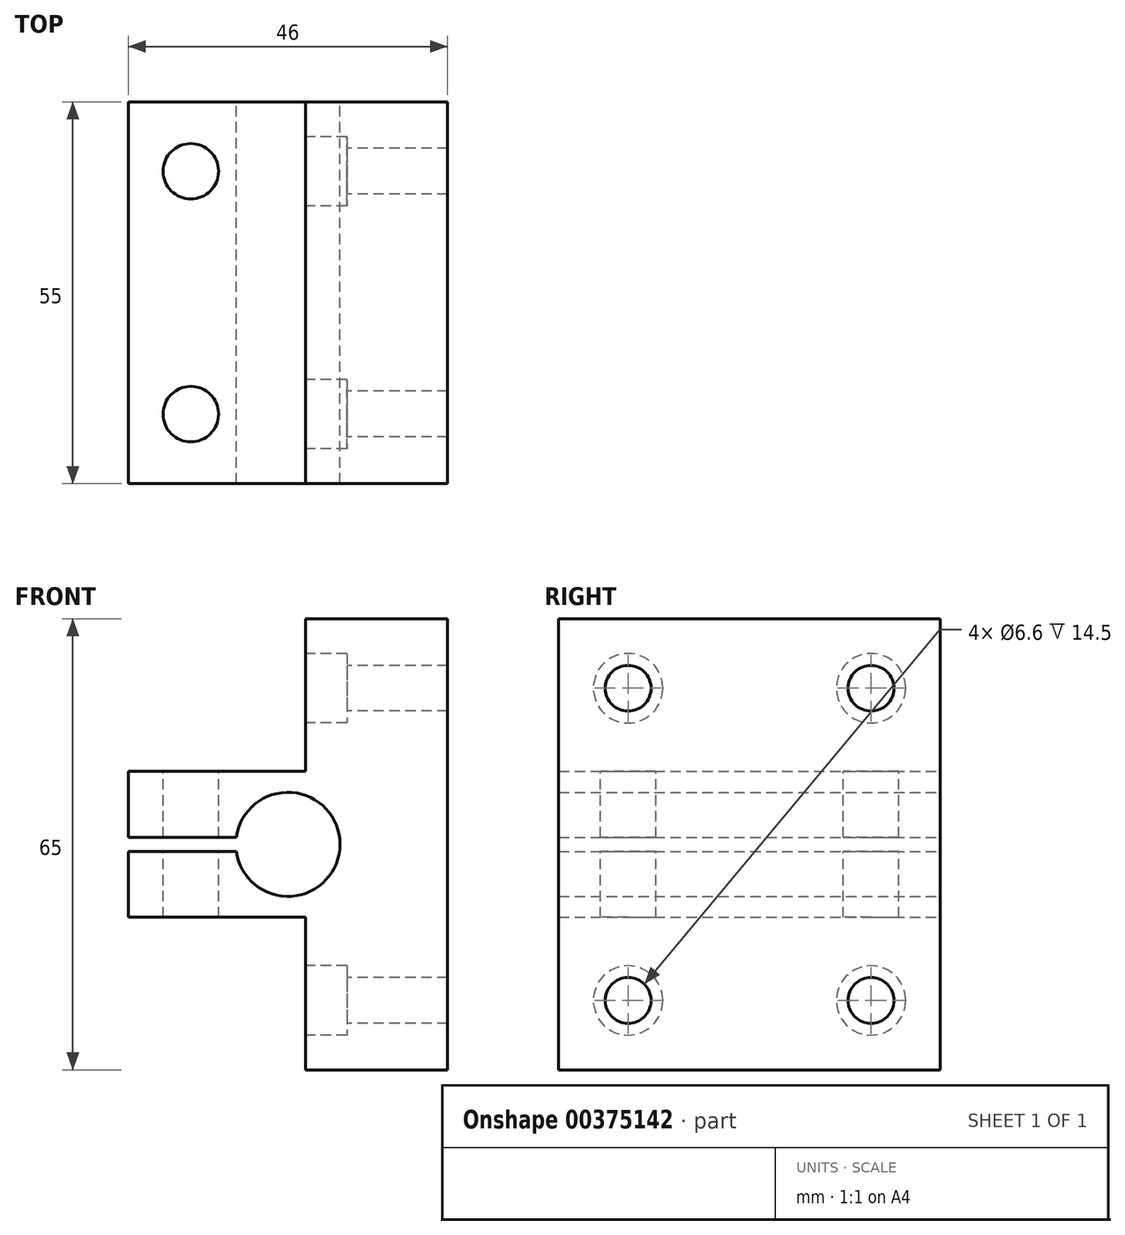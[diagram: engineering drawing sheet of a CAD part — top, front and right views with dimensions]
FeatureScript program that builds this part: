
annotation { "Feature Type Name" : "Feature", "Feature Type Description" : "" }
export const myFeature = defineFeature(function(context is Context, id is Id, definition is map)
    precondition{}
    {
        {
            var Q0;
            Q0=qCreatedBy(makeId("Front.planeOp"),FACE);
            var sketch = newSketch(context, id + "F0", { "sketchPlane" : qUnion([Q0])});
            skLineSegment(sketch, "E0", {"start": v(-56.82, 43) * mm, "end": v(-36.32, 43) * mm});
            skLineSegment(sketch, "E1", {"start": v(-36.32, 43) * mm, "end": v(-36.32, -22) * mm});
            skLineSegment(sketch, "E2", {"start": v(-36.32, -22) * mm, "end": v(-56.82, -22) * mm});
            skLineSegment(sketch, "E3", {"start": v(-56.82, -22) * mm, "end": v(-56.82, 0) * mm});
            skLineSegment(sketch, "E4", {"start": v(-56.82, 43) * mm, "end": v(-56.82, 21) * mm});
            skLineSegment(sketch, "E5", {"start": v(-56.82, 21) * mm, "end": v(-82.32, 21) * mm});
            skPoint(sketch, "E6.end.orphan", {"position": v(-82.32, 0) * mm});
            skLineSegment(sketch, "E7", {"start": v(-56.82, 0) * mm, "end": v(-82.32, 0) * mm});
            skLineSegment(sketch, "E8", {"start": v(-82.32, 0) * mm, "end": v(-82.32, 9.5) * mm});
            skLineSegment(sketch, "E9", {"start": v(-82.32, 21) * mm, "end": v(-82.32, 11.5) * mm});
            skPoint(sketch, "E10.endSnap0", {"position": v(-82.32, 10.5) * mm});
            skArc(sketch, "E11", {"start": v(-66.75, 9.5) * mm, "mid": v(-51.82, 10.5) * mm, "end": v(-66.75, 11.5) * mm});
            skLineSegment(sketch, "E12", {"start": v(-82.32, 9.5) * mm, "end": v(-66.75, 9.5) * mm});
            skLineSegment(sketch, "E13", {"start": v(-82.32, 11.5) * mm, "end": v(-66.75, 11.5) * mm});
            skSolve(sketch);
        }
        {
            var Q0;
            Q0=makeQuery(id+"F0.imprint","IMPRINT",FACE,{"disambiguationData":[TD([[makeQuery(id+"F0.imprint","IMPRINT",EDGE,{"derivedFrom":sQuery(id+"F0.wireOp",EDGE,"E0")}),-1.0]])]});
            extrude(context, id + "F1", {"entities" : qUnion([Q0]), "depth" : 55 * mm});
        }
        {
            var Q0;
            Q0=makeQuery(id+"F1.opExtrude","SWEPT_FACE",FACE,{"disambiguationData":[OSD([sQuery(id+"F0.wireOp",EDGE,"E5")])]});
            var sketch = newSketch(context, id + "F2", { "sketchPlane" : qUnion([Q0])});
            skCircle(sketch, "E14", {"center": v(-73.32, -10) * mm, "radius": 4 * mm});
            skCircle(sketch, "E15", {"center": v(-73.32, -45) * mm, "radius": 4 * mm});
            skPoint(sketch, "E16.orphan", {"position": v(-73.32, -55) * mm});
            skSolve(sketch);
        }
        {
            var Q0;
            Q0=makeQuery(id+"F2.imprint","IMPRINT",FACE,{"disambiguationData":[TD([[makeQuery(id+"F2.imprint","IMPRINT",EDGE,{"derivedFrom":sQuery(id+"F2.wireOp",EDGE,"E14")}),1.0]])]});
            var Q1;
            Q1=makeQuery(id+"F2.imprint","IMPRINT",FACE,{"disambiguationData":[TD([[makeQuery(id+"F2.imprint","IMPRINT",EDGE,{"derivedFrom":sQuery(id+"F2.wireOp",EDGE,"E15")}),1.0]])]});
            extrude(context, id + "F3", {"entities" : qUnion([Q0, Q1]), "operationType" : NewBodyOperationType.REMOVE, "oppositeDirection" : true, "depth" : 25 * mm});
        }
        {
            var Q0;
            Q0=makeQuery(id+"F1.opExtrude","SWEPT_FACE",FACE,{"disambiguationData":[OSD([sQuery(id+"F0.wireOp",EDGE,"E3")])]});
            var sketch = newSketch(context, id + "F4", { "sketchPlane" : qUnion([Q0])});
            skCircle(sketch, "E17", {"center": v(45, -12) * mm, "radius": 3.3 * mm});
            skCircle(sketch, "E18", {"center": v(45, -12) * mm, "radius": 5 * mm});
            skCircle(sketch, "E19", {"center": v(10, -12) * mm, "radius": 3.3 * mm});
            skCircle(sketch, "E20", {"center": v(10, -12) * mm, "radius": 5 * mm});
            skSolve(sketch);
        }
        {
            var Q0;
            Q0=makeQuery(id+"F4.imprint","IMPRINT",FACE,{"disambiguationData":[TD([[makeQuery(id+"F4.imprint","IMPRINT",EDGE,{"derivedFrom":sQuery(id+"F4.wireOp",EDGE,"E19")}),-1.0]])]});
            var Q1;
            Q1=makeQuery(id+"F4.imprint","IMPRINT",FACE,{"disambiguationData":[TD([[makeQuery(id+"F4.imprint","IMPRINT",EDGE,{"derivedFrom":sQuery(id+"F4.wireOp",EDGE,"E19")}),1.0]])]});
            var Q2;
            Q2=makeQuery(id+"F4.imprint","IMPRINT",FACE,{"disambiguationData":[TD([[makeQuery(id+"F4.imprint","IMPRINT",EDGE,{"derivedFrom":sQuery(id+"F4.wireOp",EDGE,"E17")}),1.0]])]});
            var Q3;
            Q3=makeQuery(id+"F4.imprint","IMPRINT",FACE,{"disambiguationData":[TD([[makeQuery(id+"F4.imprint","IMPRINT",EDGE,{"derivedFrom":sQuery(id+"F4.wireOp",EDGE,"E17")}),-1.0]])]});
            extrude(context, id + "F5", {"entities" : qUnion([Q0, Q1, Q2, Q3]), "operationType" : NewBodyOperationType.REMOVE, "oppositeDirection" : true, "depth" : 6 * mm});
        }
        {
            var Q0;
            Q0=makeQuery(id+"F4.imprint","IMPRINT",FACE,{"disambiguationData":[TD([[makeQuery(id+"F4.imprint","IMPRINT",EDGE,{"derivedFrom":sQuery(id+"F4.wireOp",EDGE,"E19")}),1.0]])]});
            var Q1;
            Q1=makeQuery(id+"F4.imprint","IMPRINT",FACE,{"disambiguationData":[TD([[makeQuery(id+"F4.imprint","IMPRINT",EDGE,{"derivedFrom":sQuery(id+"F4.wireOp",EDGE,"E17")}),1.0]])]});
            extrude(context, id + "F6", {"entities" : qUnion([Q0, Q1]), "operationType" : NewBodyOperationType.REMOVE, "oppositeDirection" : true, "depth" : 25 * mm});
        }
        {
            var Q0;
            Q0=makeQuery(id+"F1.opExtrude","SWEPT_FACE",FACE,{"disambiguationData":[OSD([sQuery(id+"F0.wireOp",EDGE,"E4")])]});
            var sketch = newSketch(context, id + "F7", { "sketchPlane" : qUnion([Q0])});
            skCircle(sketch, "E21", {"center": v(10, 33) * mm, "radius": 3.3 * mm});
            skCircle(sketch, "E22", {"center": v(10, 33) * mm, "radius": 5 * mm});
            skCircle(sketch, "E23", {"center": v(45, 33) * mm, "radius": 3.3 * mm});
            skCircle(sketch, "E24", {"center": v(45, 33) * mm, "radius": 5 * mm});
            skSolve(sketch);
        }
        {
            var Q0;
            Q0=makeQuery(id+"F7.imprint","IMPRINT",FACE,{"disambiguationData":[TD([[makeQuery(id+"F7.imprint","IMPRINT",EDGE,{"derivedFrom":sQuery(id+"F7.wireOp",EDGE,"E21")}),-1.0]])]});
            var Q1;
            Q1=makeQuery(id+"F7.imprint","IMPRINT",FACE,{"disambiguationData":[TD([[makeQuery(id+"F7.imprint","IMPRINT",EDGE,{"derivedFrom":sQuery(id+"F7.wireOp",EDGE,"E23")}),-1.0]])]});
            extrude(context, id + "F8", {"entities" : qUnion([Q0, Q1]), "operationType" : NewBodyOperationType.REMOVE, "oppositeDirection" : true, "depth" : 6 * mm});
        }
        {
            var Q0;
            Q0=makeQuery(id+"F7.imprint","IMPRINT",FACE,{"disambiguationData":[TD([[makeQuery(id+"F7.imprint","IMPRINT",EDGE,{"derivedFrom":sQuery(id+"F7.wireOp",EDGE,"E21")}),1.0]])]});
            var Q1;
            Q1=makeQuery(id+"F7.imprint","IMPRINT",FACE,{"disambiguationData":[TD([[makeQuery(id+"F7.imprint","IMPRINT",EDGE,{"derivedFrom":sQuery(id+"F7.wireOp",EDGE,"E23")}),1.0]])]});
            extrude(context, id + "F9", {"entities" : qUnion([Q0, Q1]), "operationType" : NewBodyOperationType.REMOVE, "oppositeDirection" : true, "depth" : 25 * mm});
        }
    });
